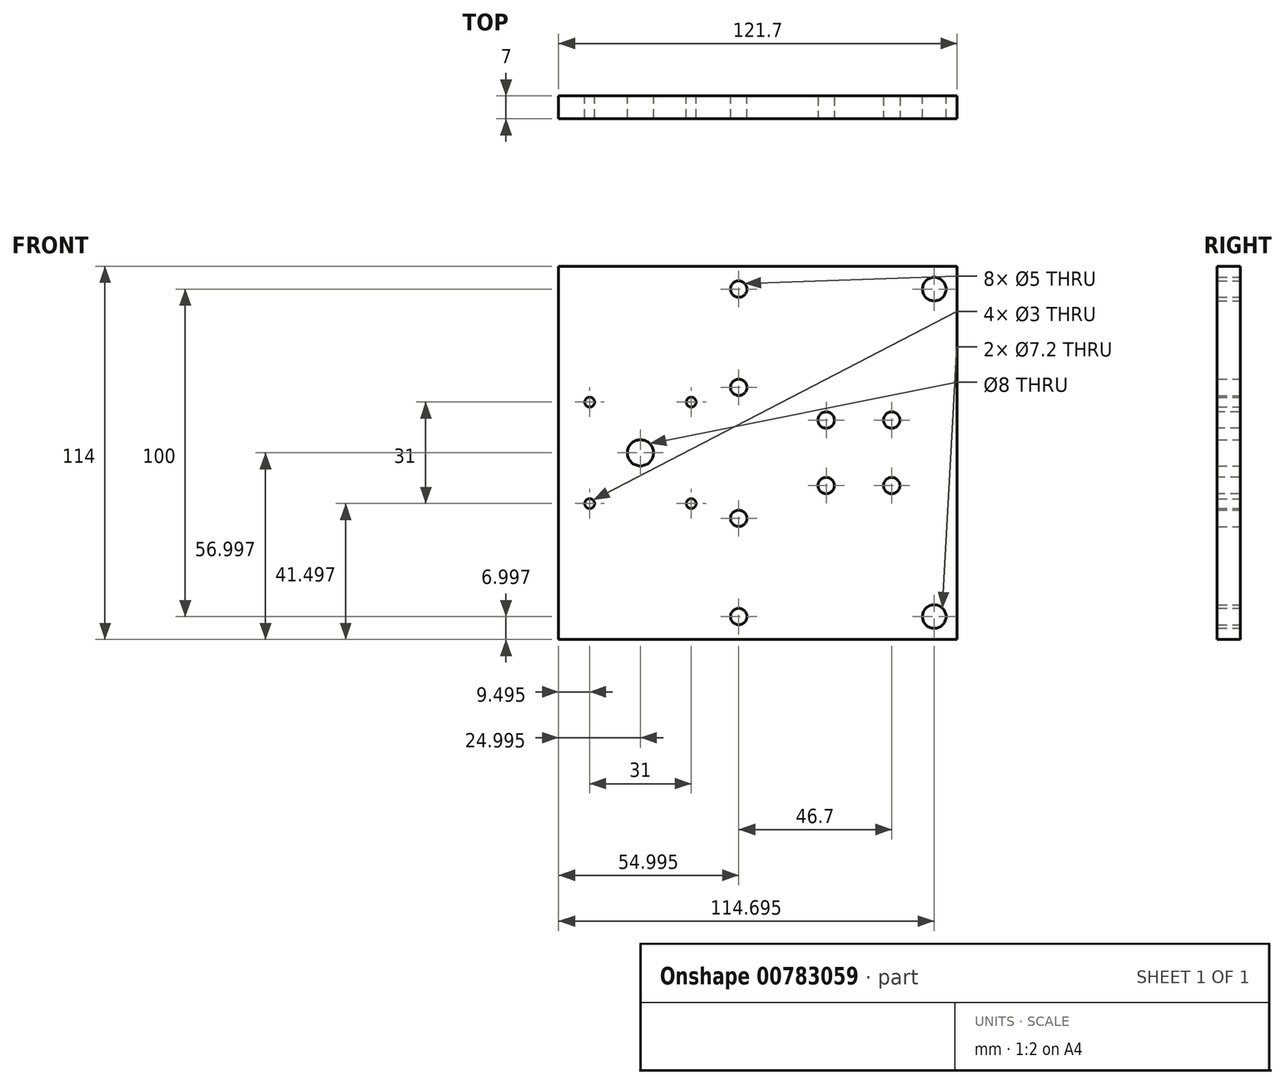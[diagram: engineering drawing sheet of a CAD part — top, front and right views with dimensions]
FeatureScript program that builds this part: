
annotation { "Feature Type Name" : "Feature", "Feature Type Description" : "" }
export const myFeature = defineFeature(function(context is Context, id is Id, definition is map)
    precondition{}
    {
        {
            var Q0;
            Q0=qCreatedBy(makeId("Front.planeOp"),FACE);
            var sketch = newSketch(context, id + "F0", { "sketchPlane" : qUnion([Q0])});
            skLineSegment(sketch, "E0.bottom", {"start": v(-116.94, 93.54) * mm, "end": v(4.76, 93.54) * mm});
            skLineSegment(sketch, "E0.top", {"start": v(-116.94, -20.46) * mm, "end": v(4.76, -20.46) * mm});
            skLineSegment(sketch, "E0.left", {"start": v(-116.94, 93.54) * mm, "end": v(-116.94, -20.46) * mm});
            skLineSegment(sketch, "E0.right", {"start": v(4.76, 93.54) * mm, "end": v(4.76, -20.46) * mm});
            skCircle(sketch, "E1", {"center": v(-61.94, -13.46) * mm, "radius": 2.5 * mm});
            skCircle(sketch, "E2", {"center": v(-2.24, -13.46) * mm, "radius": 3.6 * mm});
            skCircle(sketch, "E3.0.1.0", {"center": v(-61.94, 86.54) * mm, "radius": 2.5 * mm});
            skCircle(sketch, "E3.0.1.1", {"center": v(-2.24, 86.54) * mm, "radius": 3.6 * mm});
            skLineSegment(sketch, "E3.direction1", {"start": v(-61.94, -13.46) * mm, "end": v(-36.94, -13.46) * mm, "construction": true});
            skLineSegment(sketch, "E3.direction2", {"start": v(-61.94, -13.46) * mm, "end": v(-61.94, 86.54) * mm, "construction": true});
            skCircle(sketch, "E4", {"center": v(-91.94, 36.54) * mm, "radius": 11 * mm});
            skCircle(sketch, "E5", {"center": v(-76.44, 52.04) * mm, "radius": 1.5 * mm});
            skCircle(sketch, "E6", {"center": v(-76.44, 21.04) * mm, "radius": 1.5 * mm});
            skCircle(sketch, "E7", {"center": v(-107.44, 21.04) * mm, "radius": 1.5 * mm});
            skCircle(sketch, "E8", {"center": v(-107.44, 52.04) * mm, "radius": 1.5 * mm});
            skCircle(sketch, "E9", {"center": v(-61.94, 56.54) * mm, "radius": 2.5 * mm});
            skCircle(sketch, "E10", {"center": v(-61.94, 16.54) * mm, "radius": 2.5 * mm});
            skCircle(sketch, "E11", {"center": v(-91.94, 36.54) * mm, "radius": 4 * mm});
            skSolve(sketch);
        }
        {
            var Q0;
            Q0=makeQuery(id+"F0.imprint","IMPRINT",FACE,{"disambiguationData":[TD([[makeQuery(id+"F0.imprint","IMPRINT",EDGE,{"derivedFrom":sQuery(id+"F0.wireOp",EDGE,"E0.bottom")}),-1.0]])]});
            var Q1;
            Q1=makeQuery(id+"F0.imprint","IMPRINT",FACE,{"disambiguationData":[TD([[makeQuery(id+"F0.imprint","IMPRINT",EDGE,{"derivedFrom":sQuery(id+"F0.wireOp",EDGE,"E4")}),1.0]])]});
            extrude(context, id + "F1", {"entities" : qUnion([Q0, Q1]), "depth" : 7 * mm, "offsetDistance" : 25 * mm});
        }
        {
            var Q0;
            Q0=makeQuery(id+"F1.opExtrude","CAP_FACE",FACE,{"disambiguationData":[OSD([sQuery(id+"F0.wireOp",EDGE,"E0.bottom"),sQuery(id+"F0.wireOp",EDGE,"E0.top"),sQuery(id+"F0.wireOp",EDGE,"E0.left"),sQuery(id+"F0.wireOp",EDGE,"E0.right"),sQuery(id+"F0.wireOp",EDGE,"E1"),sQuery(id+"F0.wireOp",EDGE,"E2"),sQuery(id+"F0.wireOp",EDGE,"E3.0.1.0"),sQuery(id+"F0.wireOp",EDGE,"E3.0.1.1"),sQuery(id+"F0.wireOp",EDGE,"E5"),sQuery(id+"F0.wireOp",EDGE,"E6"),sQuery(id+"F0.wireOp",EDGE,"E7"),sQuery(id+"F0.wireOp",EDGE,"E8"),sQuery(id+"F0.wireOp",EDGE,"E9"),sQuery(id+"F0.wireOp",EDGE,"E10"),sQuery(id+"F0.wireOp",EDGE,"E11")])],"isStart":false});
            var sketch = newSketch(context, id + "F2", { "sketchPlane" : qUnion([Q0])});
            skCircle(sketch, "E12", {"center": v(-35.24, 46.54) * mm, "radius": 2.5 * mm});
            skCircle(sketch, "E13", {"center": v(-15.24, 46.54) * mm, "radius": 2.5 * mm});
            skCircle(sketch, "E14", {"center": v(-35.24, 26.54) * mm, "radius": 2.5 * mm});
            skCircle(sketch, "E15", {"center": v(-15.24, 26.54) * mm, "radius": 2.5 * mm});
            skSolve(sketch);
        }
        {
            var Q0;
            Q0 = qSketchRegion(id + "F2", true);
            extrude(context, id + "F3", {"entities" : qUnion([Q0]), "operationType" : NewBodyOperationType.REMOVE, "oppositeDirection" : true, "depth" : 25 * mm, "offsetDistance" : 25 * mm});
        }
    });
